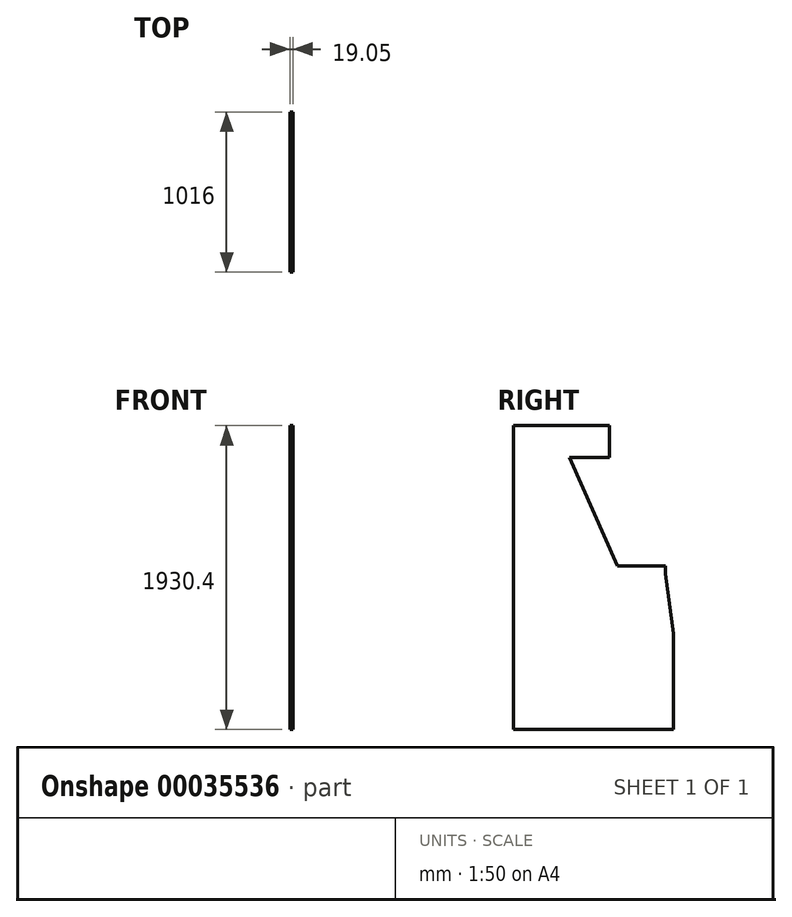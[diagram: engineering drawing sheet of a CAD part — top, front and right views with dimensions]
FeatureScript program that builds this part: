
annotation { "Feature Type Name" : "Feature", "Feature Type Description" : "" }
export const myFeature = defineFeature(function(context is Context, id is Id, definition is map)
    precondition{}
    {
        {
            var Q0;
            Q0=qCreatedBy(makeId("Right.planeOp"),FACE);
            var sketch = newSketch(context, id + "F0", { "sketchPlane" : qUnion([Q0])});
            skLineSegment(sketch, "E0", {"start": v(-761.56, 1011.91) * mm, "end": v(-761.56, -918.49) * mm});
            skLineSegment(sketch, "E1", {"start": v(-761.56, -918.49) * mm, "end": v(254.44, -918.49) * mm});
            skLineSegment(sketch, "E2", {"start": v(254.44, -918.49) * mm, "end": v(254.44, -308.89) * mm});
            skLineSegment(sketch, "E3", {"start": v(-761.56, 1011.91) * mm, "end": v(-151.96, 1011.91) * mm});
            skLineSegment(sketch, "E4", {"start": v(-151.96, 1011.91) * mm, "end": v(-151.96, 808.71) * mm});
            skLineSegment(sketch, "E5", {"start": v(-151.96, 808.71) * mm, "end": v(-405.96, 808.71) * mm});
            skLineSegment(sketch, "E6", {"start": v(-405.96, 808.71) * mm, "end": v(-101.16, 119.74) * mm});
            skLineSegment(sketch, "E7", {"start": v(-101.16, 119.74) * mm, "end": v(203.64, 119.74) * mm});
            skLineSegment(sketch, "E8", {"start": v(203.64, 119.74) * mm, "end": v(203.64, 68.94) * mm});
            skLineSegment(sketch, "E9", {"start": v(254.44, -308.89) * mm, "end": v(203.64, 68.94) * mm});
            skSolve(sketch);
        }
        {
            var Q0;
            Q0 = qSketchRegion(id + "F0", true);
            extrude(context, id + "F1", {"entities" : qUnion([Q0]), "depth" : 19.05 * mm});
        }
    });
